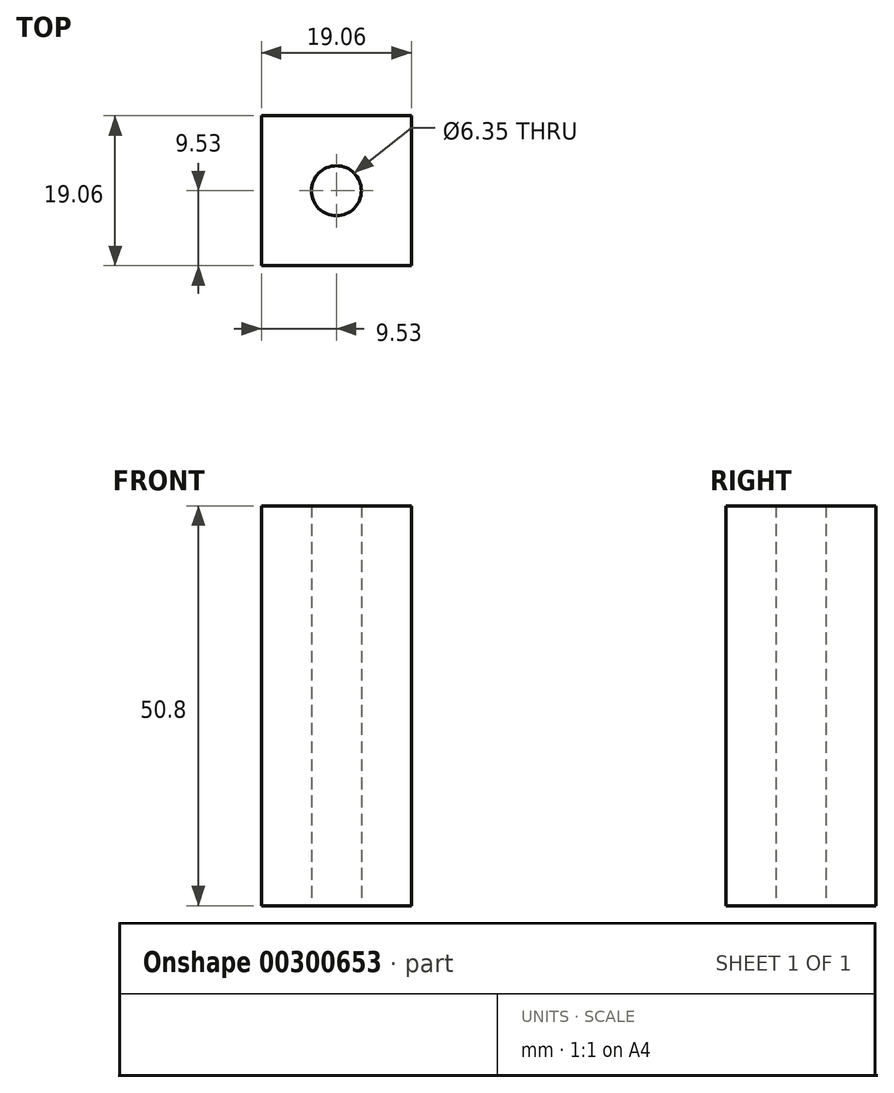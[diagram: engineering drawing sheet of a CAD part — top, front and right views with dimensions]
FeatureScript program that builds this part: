
annotation { "Feature Type Name" : "Feature", "Feature Type Description" : "" }
export const myFeature = defineFeature(function(context is Context, id is Id, definition is map)
    precondition{}
    {
        {
            var Q0;
            Q0=qCreatedBy(makeId("Top.planeOp"),FACE);
            var sketch = newSketch(context, id + "F0", { "sketchPlane" : qUnion([Q0])});
            skLineSegment(sketch, "E0", {"start": v(-9.53, 9.53) * mm, "end": v(9.53, 9.53) * mm});
            skLineSegment(sketch, "E1", {"start": v(9.53, 9.53) * mm, "end": v(9.53, -9.52) * mm});
            skLineSegment(sketch, "E2", {"start": v(9.53, -9.52) * mm, "end": v(-9.53, -9.52) * mm});
            skLineSegment(sketch, "E3", {"start": v(-9.53, -9.52) * mm, "end": v(-9.53, 9.53) * mm});
            skCircle(sketch, "E4", {"center": v(0, 0) * mm, "radius": 3.18 * mm});
            skSolve(sketch);
        }
        {
            var Q0;
            Q0 = qSketchRegion(id + "F0", true);
            extrude(context, id + "F1", {"entities" : qUnion([Q0]), "depth" : 50.8 * mm});
        }
    });
